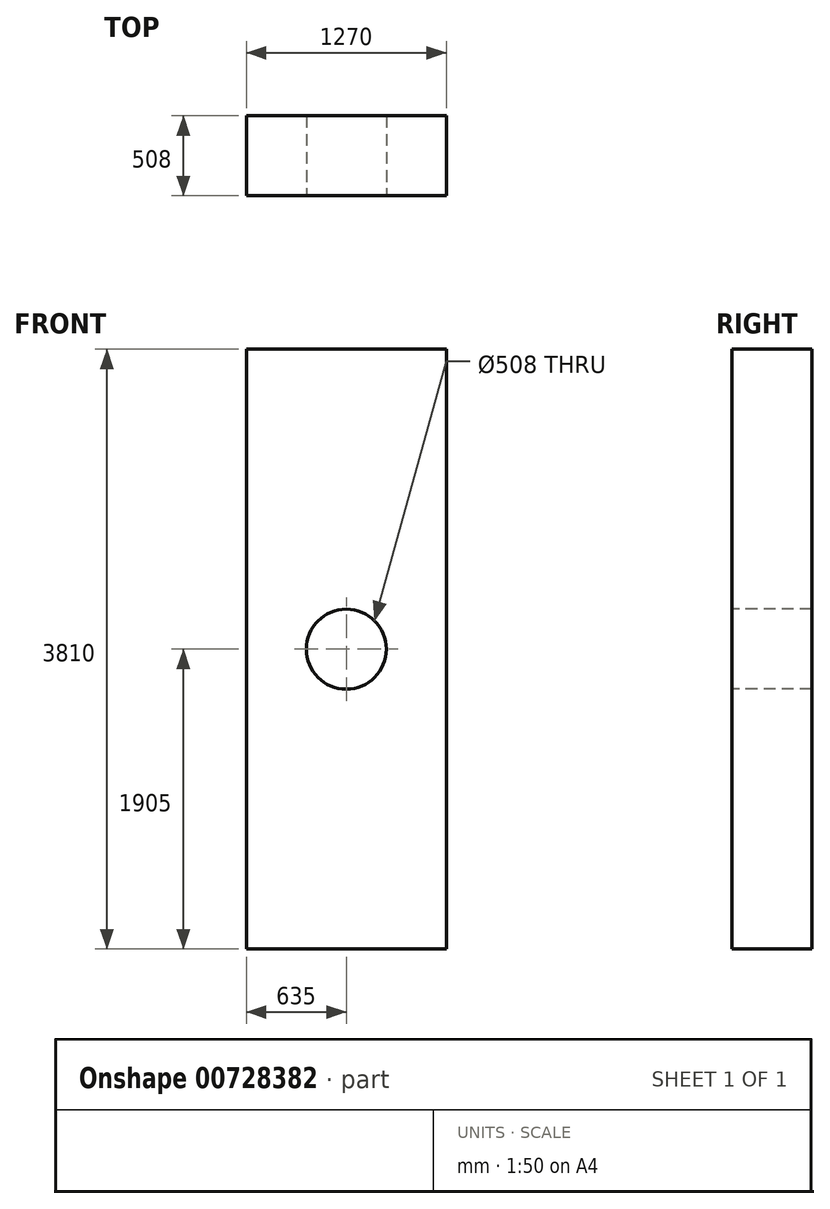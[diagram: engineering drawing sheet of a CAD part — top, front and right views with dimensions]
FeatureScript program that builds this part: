
annotation { "Feature Type Name" : "Feature", "Feature Type Description" : "" }
export const myFeature = defineFeature(function(context is Context, id is Id, definition is map)
    precondition{}
    {
        {
            var Q0;
            Q0=qCreatedBy(makeId("Top.planeOp"),FACE);
            var sketch = newSketch(context, id + "F0", { "sketchPlane" : qUnion([Q0])});
            skLineSegment(sketch, "E0.bottom", {"start": v(0, 0) * mm, "end": v(1270, 0) * mm});
            skLineSegment(sketch, "E0.top", {"start": v(0, 508) * mm, "end": v(1270, 508) * mm});
            skLineSegment(sketch, "E0.left", {"start": v(0, 0) * mm, "end": v(0, 508) * mm});
            skLineSegment(sketch, "E0.right", {"start": v(1270, 0) * mm, "end": v(1270, 508) * mm});
            skSolve(sketch);
        }
        {
            var Q0;
            Q0 = qSketchRegion(id + "F0", true);
            extrude(context, id + "F1", {"entities" : qUnion([Q0]), "depth" : 3810 * mm, "offsetDistance" : 25.4 * mm});
        }
        {
            var Q0;
            Q0=makeQuery(id+"F1.opExtrude","SWEPT_FACE",FACE,{"disambiguationData":[OSD([sQuery(id+"F0.wireOp",EDGE,"E0.bottom")])]});
            var sketch = newSketch(context, id + "F2", { "sketchPlane" : qUnion([Q0])});
            skCircle(sketch, "E1", {"center": v(635, 1905) * mm, "radius": 254 * mm});
            skPoint(sketch, "E1.centerSnap0", {"position": v(1270, 1905) * mm});
            skPoint(sketch, "E1.centerSnap1", {"position": v(635, 3810) * mm});
            skSolve(sketch);
        }
        {
            var Q0;
            Q0 = qSketchRegion(id + "F2", true);
            extrude(context, id + "F3", {"entities" : qUnion([Q0]), "operationType" : NewBodyOperationType.REMOVE, "endBound" : BoundingType.THROUGH_ALL, "oppositeDirection" : true, "depth" : 25.4 * mm, "offsetDistance" : 25.4 * mm});
        }
    });
